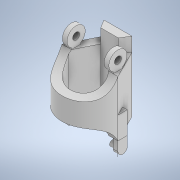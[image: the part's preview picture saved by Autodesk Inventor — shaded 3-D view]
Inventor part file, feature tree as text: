
AUTODESK INVENTOR PART (.ipt)
format: ipt  version: 2022 (Build 260153000, 153)  size: 290,816 bytes
history: native  units: mm
features: extrude x15, sketch x9, other x2, shell x1, projected_geometry x1
ambient origin geometry x8: Origin, YZ Plane, XZ Plane, XY Plane, X Axis, Y Axis, Z Axis, Center Point
bodies: Body1 (feature_tree)
feature tree (28):
  other  "솔리드1"
  extrude  "돌출1"  Depth=20.0mm
  sketch  "스케치2"
  shell  "쉘1"  Thickness=10.0mm
  extrude  "돌출3"  Depth=5.0mm
  sketch  "스케치8"
  extrude  "돌출7"  Depth=20.0mm TaperAngle=0.0deg
  sketch  "스케치9"
  extrude  "돌출8"  Depth=6.0mm
  extrude  "돌출9"  Depth=3.0mm
  sketch  "스케치11"
  extrude  "돌출10"  Depth=30.0mm TaperAngle=0.0deg
  sketch  "스케치12"
  extrude  "돌출11"  Depth=30.0mm TaperAngle=0.0deg
  extrude  "돌출12"  Depth=5.0mm TaperAngle=0.0deg
  extrude  "돌출13"  Depth=5.0mm TaperAngle=0.0deg
  sketch  "스케치14"
  extrude  "돌출15"  Depth=6.5mm
  other  "작업 평면1"
  extrude  "돌출17"  Depth=2.5mm
  extrude  "돌출18"  Depth=8.0mm TaperAngle=0.0deg
  extrude  "돌출19"  Depth=2.0mm
  extrude  "돌출20"  Depth=100.0mm TaperAngle=0.0deg
  extrude  "돌출21"  Depth=2.0mm TaperAngle=0.0deg
  sketch  "스케치1"
  sketch  "스케치13"
  projected_geometry  "투영된 루프1"
  sketch  "스케치15"
